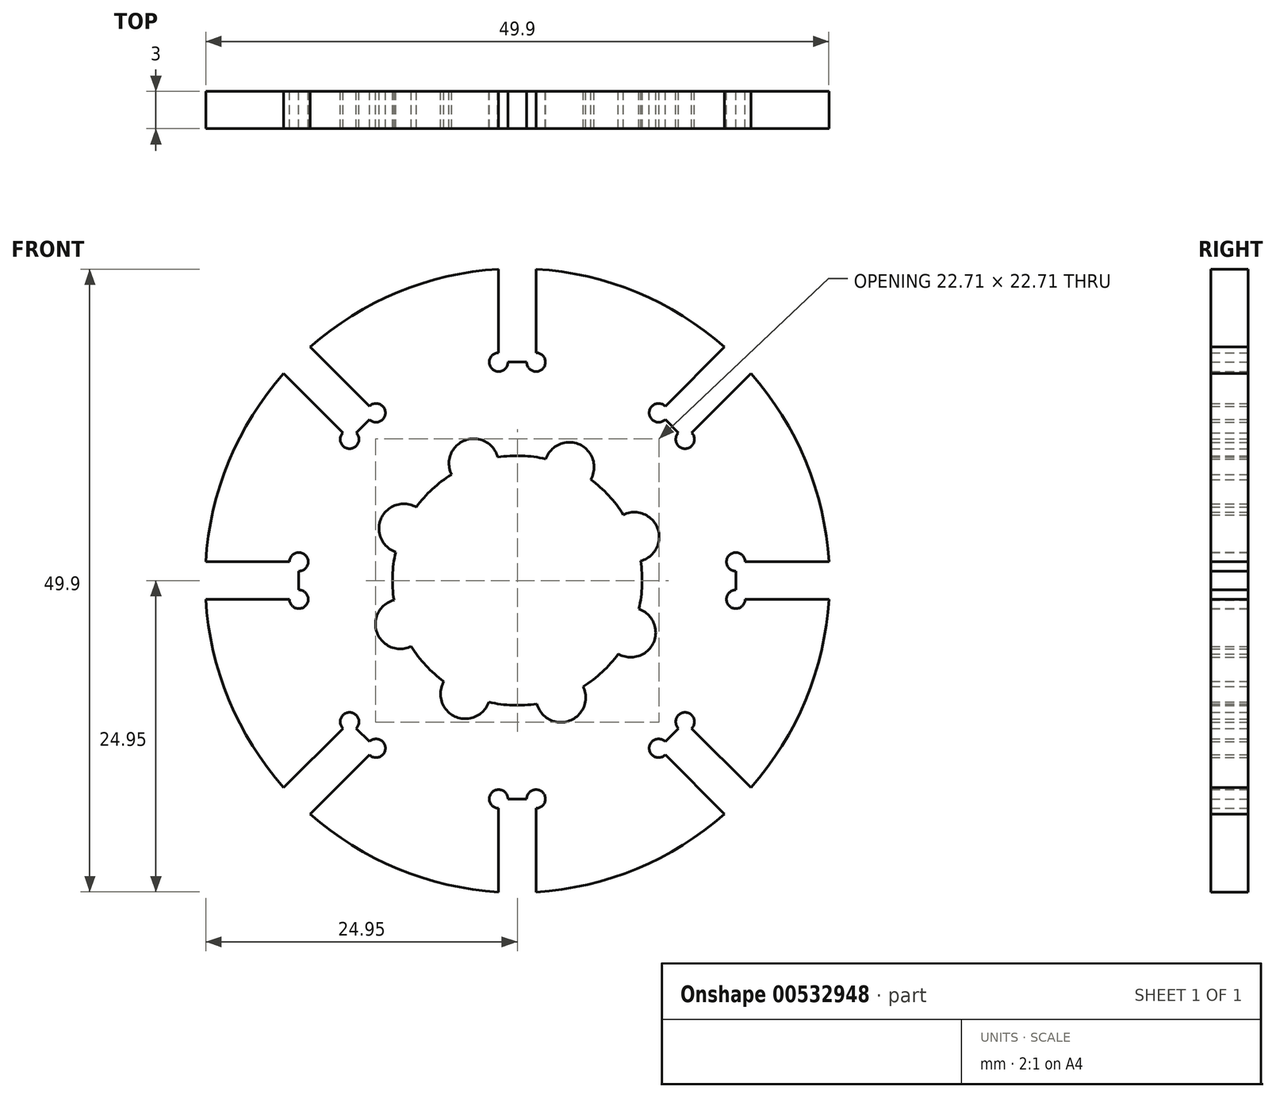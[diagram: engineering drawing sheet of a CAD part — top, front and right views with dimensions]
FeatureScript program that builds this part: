
annotation { "Feature Type Name" : "Feature", "Feature Type Description" : "" }
export const myFeature = defineFeature(function(context is Context, id is Id, definition is map)
    precondition{}
    {
        {
            assignVariable(context, id + "F0", {"name" : "w", "anyValue" : 3});
        }
        {
            var Q0;
            Q0=qCreatedBy(makeId("Front.planeOp"),FACE);
            var sketch = newSketch(context, id + "F1", { "sketchPlane" : qUnion([Q0])});
            skCircle(sketch, "E0", {"center": v(0, 0) * mm, "radius": 25 * mm});
            skLineSegment(sketch, "E1.bottom", {"start": v(1.5, 17.5) * mm, "end": v(-1.5, 17.5) * mm});
            skLineSegment(sketch, "E1.top", {"start": v(1.5, 32.5) * mm, "end": v(-1.5, 32.5) * mm});
            skLineSegment(sketch, "E1.left", {"start": v(1.5, 17.5) * mm, "end": v(1.5, 32.5) * mm});
            skLineSegment(sketch, "E1.right", {"start": v(-1.5, 17.5) * mm, "end": v(-1.5, 32.5) * mm});
            skPoint(sketch, "E1.middle", {"position": v(0, 25) * mm});
            skLineSegment(sketch, "E2.1.0", {"start": v(-11.31, 13.44) * mm, "end": v(-21.92, 24.04) * mm});
            skLineSegment(sketch, "E2.1.1", {"start": v(-11.31, 13.44) * mm, "end": v(-13.44, 11.31) * mm});
            skLineSegment(sketch, "E2.1.2", {"start": v(-13.44, 11.31) * mm, "end": v(-24.04, 21.92) * mm});
            skLineSegment(sketch, "E2.1.3", {"start": v(-21.92, 24.04) * mm, "end": v(-24.04, 21.92) * mm});
            skLineSegment(sketch, "E2.2.0", {"start": v(-17.5, 1.5) * mm, "end": v(-32.5, 1.5) * mm});
            skLineSegment(sketch, "E2.2.1", {"start": v(-17.5, 1.5) * mm, "end": v(-17.5, -1.5) * mm});
            skLineSegment(sketch, "E2.2.2", {"start": v(-17.5, -1.5) * mm, "end": v(-32.5, -1.5) * mm});
            skLineSegment(sketch, "E2.2.3", {"start": v(-32.5, 1.5) * mm, "end": v(-32.5, -1.5) * mm});
            skLineSegment(sketch, "E2.3.0", {"start": v(-13.44, -11.31) * mm, "end": v(-24.04, -21.92) * mm});
            skLineSegment(sketch, "E2.3.1", {"start": v(-13.44, -11.31) * mm, "end": v(-11.31, -13.44) * mm});
            skLineSegment(sketch, "E2.3.2", {"start": v(-11.31, -13.44) * mm, "end": v(-21.92, -24.04) * mm});
            skLineSegment(sketch, "E2.3.3", {"start": v(-24.04, -21.92) * mm, "end": v(-21.92, -24.04) * mm});
            skLineSegment(sketch, "E2.4.0", {"start": v(-1.5, -17.5) * mm, "end": v(-1.5, -32.5) * mm});
            skLineSegment(sketch, "E2.4.1", {"start": v(-1.5, -17.5) * mm, "end": v(1.5, -17.5) * mm});
            skLineSegment(sketch, "E2.4.2", {"start": v(1.5, -17.5) * mm, "end": v(1.5, -32.5) * mm});
            skLineSegment(sketch, "E2.4.3", {"start": v(-1.5, -32.5) * mm, "end": v(1.5, -32.5) * mm});
            skLineSegment(sketch, "E2.5.0", {"start": v(11.31, -13.44) * mm, "end": v(21.92, -24.04) * mm});
            skLineSegment(sketch, "E2.5.1", {"start": v(11.31, -13.44) * mm, "end": v(13.44, -11.31) * mm});
            skLineSegment(sketch, "E2.5.2", {"start": v(13.44, -11.31) * mm, "end": v(24.04, -21.92) * mm});
            skLineSegment(sketch, "E2.5.3", {"start": v(21.92, -24.04) * mm, "end": v(24.04, -21.92) * mm});
            skLineSegment(sketch, "E2.6.0", {"start": v(17.5, -1.5) * mm, "end": v(32.5, -1.5) * mm});
            skLineSegment(sketch, "E2.6.1", {"start": v(17.5, -1.5) * mm, "end": v(17.5, 1.5) * mm});
            skLineSegment(sketch, "E2.6.2", {"start": v(17.5, 1.5) * mm, "end": v(32.5, 1.5) * mm});
            skLineSegment(sketch, "E2.6.3", {"start": v(32.5, -1.5) * mm, "end": v(32.5, 1.5) * mm});
            skLineSegment(sketch, "E2.7.0", {"start": v(13.44, 11.31) * mm, "end": v(24.04, 21.92) * mm});
            skLineSegment(sketch, "E2.7.1", {"start": v(13.44, 11.31) * mm, "end": v(11.31, 13.44) * mm});
            skLineSegment(sketch, "E2.7.2", {"start": v(11.31, 13.44) * mm, "end": v(21.92, 24.04) * mm});
            skLineSegment(sketch, "E2.7.3", {"start": v(24.04, 21.92) * mm, "end": v(21.92, 24.04) * mm});
            skCircle(sketch, "E3", {"center": v(0, 0) * mm, "radius": 10 * mm});
            skCircle(sketch, "E4", {"center": v(4.16, 9.1) * mm, "radius": 1.99 * mm});
            skCircle(sketch, "E5.1.0", {"center": v(-3.49, 9.37) * mm, "radius": 1.99 * mm});
            skCircle(sketch, "E5.2.0", {"center": v(-9.1, 4.16) * mm, "radius": 1.99 * mm});
            skCircle(sketch, "E5.3.0", {"center": v(-9.37, -3.49) * mm, "radius": 1.99 * mm});
            skCircle(sketch, "E5.4.0", {"center": v(-4.16, -9.1) * mm, "radius": 1.99 * mm});
            skCircle(sketch, "E5.5.0", {"center": v(3.49, -9.37) * mm, "radius": 1.99 * mm});
            skCircle(sketch, "E5.6.0", {"center": v(9.1, -4.16) * mm, "radius": 1.99 * mm});
            skCircle(sketch, "E5.7.0", {"center": v(9.37, 3.49) * mm, "radius": 1.99 * mm});
            skCircle(sketch, "E6", {"center": v(1.5, 17.5) * mm, "radius": 0.75 * mm});
            skCircle(sketch, "E7", {"center": v(-1.5, 17.5) * mm, "radius": 0.75 * mm});
            skCircle(sketch, "E8.1.0", {"center": v(-11.31, 13.44) * mm, "radius": 0.75 * mm});
            skCircle(sketch, "E8.1.1", {"center": v(-13.44, 11.31) * mm, "radius": 0.75 * mm});
            skCircle(sketch, "E8.2.0", {"center": v(-17.5, 1.5) * mm, "radius": 0.75 * mm});
            skCircle(sketch, "E8.2.1", {"center": v(-17.5, -1.5) * mm, "radius": 0.75 * mm});
            skCircle(sketch, "E8.3.0", {"center": v(-13.44, -11.31) * mm, "radius": 0.75 * mm});
            skCircle(sketch, "E8.3.1", {"center": v(-11.31, -13.44) * mm, "radius": 0.75 * mm});
            skCircle(sketch, "E8.4.0", {"center": v(-1.5, -17.5) * mm, "radius": 0.75 * mm});
            skCircle(sketch, "E8.4.1", {"center": v(1.5, -17.5) * mm, "radius": 0.75 * mm});
            skCircle(sketch, "E8.5.0", {"center": v(11.31, -13.44) * mm, "radius": 0.75 * mm});
            skCircle(sketch, "E8.5.1", {"center": v(13.44, -11.31) * mm, "radius": 0.75 * mm});
            skCircle(sketch, "E8.6.0", {"center": v(17.5, -1.5) * mm, "radius": 0.75 * mm});
            skCircle(sketch, "E8.6.1", {"center": v(17.5, 1.5) * mm, "radius": 0.75 * mm});
            skCircle(sketch, "E8.7.0", {"center": v(13.44, 11.31) * mm, "radius": 0.75 * mm});
            skCircle(sketch, "E8.7.1", {"center": v(11.31, 13.44) * mm, "radius": 0.75 * mm});
            skSolve(sketch);
        }
        {
            var Q0;
            {var subQ13=sQuery(id+"F1.wireOp",EDGE,"E0");var subQ75=sQuery(id+"F1.wireOp",EDGE,"E2.7.0");var subQ92=makeQuery(id+"F1.imprint","INTERSECT",VERTEX,{"derivedFrom":[subQ13,subQ75]});Q0=makeQuery(id+"F1.imprint","IMPRINT",FACE,{"disambiguationData":[TD([[makeQuery(id+"F1.imprint","IMPRINT",EDGE,{"disambiguationData":[TD([[subQ92,1.0]])],"derivedFrom":subQ13}),1.0]])]});}
            extrude(context, id + "F2", {"entities" : qUnion([Q0]), "depth" : (getVariable(context, 'w')) * mm, "offsetDistance" : 25 * mm});
        }
    });
